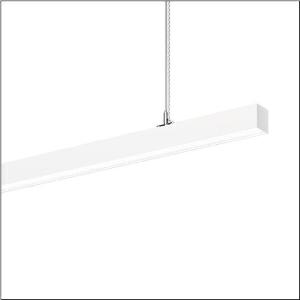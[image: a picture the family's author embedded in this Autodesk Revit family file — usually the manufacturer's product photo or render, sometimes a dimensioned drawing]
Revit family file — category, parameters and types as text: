
# Revit family: silica_r__21_51mx33da37wb_a2a9
name_source: partatom
category: Lighting Fixtures
units: mm (PartAtom-declared; Revit-internal decimal feet)

## family parameters
Cut with Voids When Loaded = No
Host = Face
Light Source = No
Part Type = Normal
Room Calculation Point = No
Round Connector Dimension = Use Diameter
Shared = No

## types (1)
- --- (1 x LED, 5910 lm, 41.3 W, 3000K)
    Apparent Load = 41 VA
    CIE Flux Codes = 78 96 99 55 100
    Color Rendering = 80
    Color Temperature = 3000K
    Default Elevation = 1800 mm
    Description = Silica® 21, office luminaire, primary optical cover: prismatic diffuser, of PMMA, CAT 2 (L<= 3000cd/m²), light emission: direct/indirect distribution, primary light characteristic: symmetric, installation type: suspended mounting, LED, rated luminous flux: 5.910lm, luminous efficacy: 143lm/W, light colour: 830, colour temperature: 3000K, control gear: DALI 2, with terminal, 3+2-pole, max. 2.5mm², mains connection: 220..240V, AC, 50/60Hz, rated input power: 41.3W, luminaire housing, of aluminium, traffic white (RAL 9016), length: 1.204mm, width: 53mm, height: 53mm, protection rating (complete): IP20, insulation class (complete): insulation class I (protective earthing), certification: CE, permissible operating ambient temperature: 0..+35°C, standard: EN 50419, packaging unit: 1 piece
    Height = 53 mm
    Lamp = 1 x LED
    Lamp Light Flux = 5910 lm
    Lamp Power = 41.3 W
    Lamp count = 1
    Length = 1204 mm
    Luminous efficacy = 143 lm/W
    Manufacturer = Siteco
    ModVariant = No
    Model = 51MX33DA37WB
    Mounting Place = Ceiling
    Mounting Type = Pendant
    Number of Poles = 1
    OnlyDefault = Yes
    Power Factor = 1
    Product Name = Silica® 21
    Product group = office luminaire | ceiling pendant
    ProductGroupID = 903
    Protection Class = Protection class I
    Protection Degree = IP 20
    RLX_Detail_Level = 1
    RLX_Emergency_Light_Flux = 0 lm
    RLX_Emergency_Type = 0
    RLX_Emergency_Type_DB = No
    RlxData = <blob elided: 21381 chars, md5=266757fe>
    Socket = socket
    Standby Power = 0 W
    System Light Flux = 5910 lm
    System Power = 41 W
    Type Comments = factory setting: luminous flux: 100 % | dim-lin: 254 | 345 mA
    Type Image = l_1349007.jpg
    URL = http://relux.com
    VarID = @adj_122827
    Voltage = 0 V
    Weight = 0.00 kg
    Width = 53 mm

## geometry (parser evidence)
native form markers: Blend x4, Sweep x12
no freeform markers — native parametric forms only
